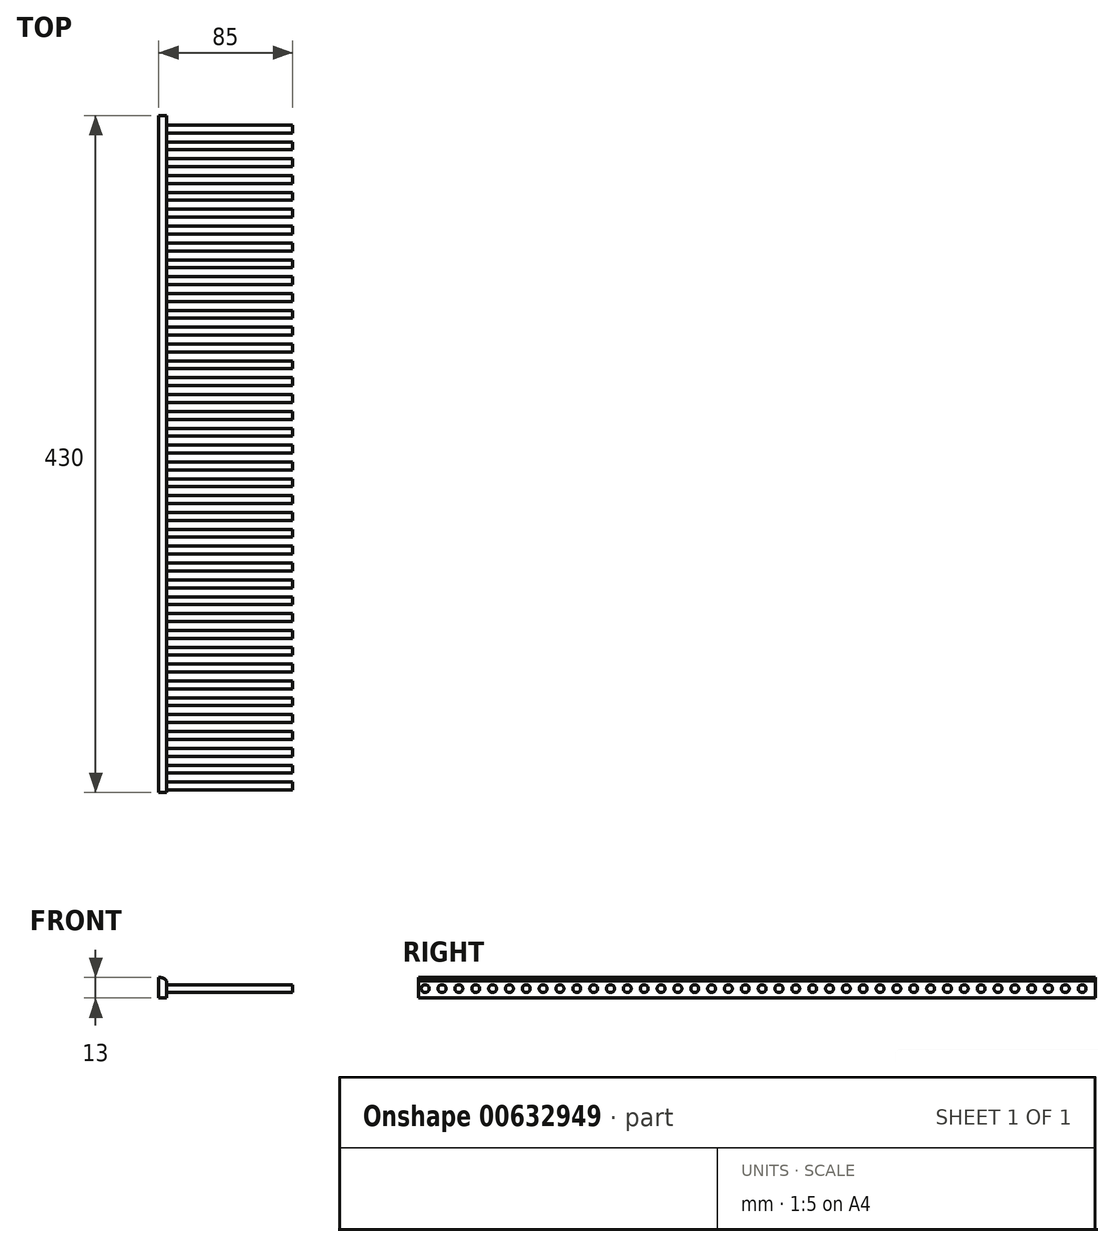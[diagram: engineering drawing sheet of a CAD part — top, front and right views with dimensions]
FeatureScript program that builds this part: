
annotation { "Feature Type Name" : "Feature", "Feature Type Description" : "" }
export const myFeature = defineFeature(function(context is Context, id is Id, definition is map)
    precondition{}
    {
        {
            var Q0;
            Q0=qCreatedBy(makeId("Right.planeOp"),FACE);
            var sketch = newSketch(context, id + "F0", { "sketchPlane" : qUnion([Q0])});
            skLineSegment(sketch, "E0.bottom", {"start": v(-215, 10.84) * mm, "end": v(215, 10.84) * mm});
            skLineSegment(sketch, "E0.top", {"start": v(-215, -2.16) * mm, "end": v(215, -2.16) * mm});
            skLineSegment(sketch, "E0.left", {"start": v(-215, 10.84) * mm, "end": v(-215, -2.16) * mm});
            skLineSegment(sketch, "E0.right", {"start": v(215, 10.84) * mm, "end": v(215, -2.16) * mm});
            skLineSegment(sketch, "E1", {"start": v(-215, 3.84) * mm, "end": v(215, 3.84) * mm, "construction": true});
            skCircle(sketch, "E2", {"center": v(206.5, 3.84) * mm, "radius": 2.5 * mm});
            skCircle(sketch, "E3", {"center": v(195.8, 3.84) * mm, "radius": 2.5 * mm});
            skCircle(sketch, "E4", {"center": v(185.1, 3.84) * mm, "radius": 2.5 * mm});
            skCircle(sketch, "E5", {"center": v(174.4, 3.84) * mm, "radius": 2.5 * mm});
            skCircle(sketch, "E6", {"center": v(163.7, 3.84) * mm, "radius": 2.5 * mm});
            skCircle(sketch, "E7", {"center": v(153, 3.84) * mm, "radius": 2.5 * mm});
            skCircle(sketch, "E8", {"center": v(142.3, 3.84) * mm, "radius": 2.5 * mm});
            skCircle(sketch, "E9", {"center": v(131.6, 3.84) * mm, "radius": 2.5 * mm});
            skCircle(sketch, "E10", {"center": v(120.9, 3.84) * mm, "radius": 2.5 * mm});
            skCircle(sketch, "E11", {"center": v(110.2, 3.84) * mm, "radius": 2.5 * mm});
            skCircle(sketch, "E12", {"center": v(99.5, 3.84) * mm, "radius": 2.5 * mm});
            skCircle(sketch, "E13", {"center": v(88.8, 3.84) * mm, "radius": 2.5 * mm});
            skCircle(sketch, "E14", {"center": v(78.1, 3.84) * mm, "radius": 2.5 * mm});
            skCircle(sketch, "E15", {"center": v(67.4, 3.84) * mm, "radius": 2.5 * mm});
            skCircle(sketch, "E16", {"center": v(56.7, 3.84) * mm, "radius": 2.5 * mm});
            skCircle(sketch, "E17", {"center": v(46, 3.84) * mm, "radius": 2.5 * mm});
            skCircle(sketch, "E18", {"center": v(35.3, 3.84) * mm, "radius": 2.5 * mm});
            skCircle(sketch, "E19", {"center": v(24.6, 3.84) * mm, "radius": 2.5 * mm});
            skCircle(sketch, "E20", {"center": v(13.9, 3.84) * mm, "radius": 2.5 * mm});
            skCircle(sketch, "E21", {"center": v(3.2, 3.84) * mm, "radius": 2.5 * mm});
            skCircle(sketch, "E22", {"center": v(-7.5, 3.84) * mm, "radius": 2.5 * mm});
            skCircle(sketch, "E23", {"center": v(-18.2, 3.84) * mm, "radius": 2.5 * mm});
            skCircle(sketch, "E24", {"center": v(-28.9, 3.84) * mm, "radius": 2.5 * mm});
            skCircle(sketch, "E25", {"center": v(-39.6, 3.84) * mm, "radius": 2.5 * mm});
            skCircle(sketch, "E26", {"center": v(-50.3, 3.84) * mm, "radius": 2.5 * mm});
            skCircle(sketch, "E27", {"center": v(-61, 3.84) * mm, "radius": 2.5 * mm});
            skCircle(sketch, "E28", {"center": v(-71.7, 3.84) * mm, "radius": 2.5 * mm});
            skCircle(sketch, "E29", {"center": v(-82.4, 3.84) * mm, "radius": 2.5 * mm});
            skCircle(sketch, "E30", {"center": v(-93.1, 3.84) * mm, "radius": 2.5 * mm});
            skCircle(sketch, "E31", {"center": v(-103.8, 3.84) * mm, "radius": 2.5 * mm});
            skCircle(sketch, "E32", {"center": v(-114.5, 3.84) * mm, "radius": 2.5 * mm});
            skCircle(sketch, "E33", {"center": v(-125.2, 3.84) * mm, "radius": 2.5 * mm});
            skCircle(sketch, "E34", {"center": v(-135.9, 3.84) * mm, "radius": 2.5 * mm});
            skCircle(sketch, "E35", {"center": v(-146.6, 3.84) * mm, "radius": 2.5 * mm});
            skCircle(sketch, "E36", {"center": v(-157.3, 3.84) * mm, "radius": 2.5 * mm});
            skCircle(sketch, "E37", {"center": v(-168, 3.84) * mm, "radius": 2.5 * mm});
            skCircle(sketch, "E38", {"center": v(-178.7, 3.84) * mm, "radius": 2.5 * mm});
            skCircle(sketch, "E39", {"center": v(-189.4, 3.84) * mm, "radius": 2.5 * mm});
            skCircle(sketch, "E40", {"center": v(-200.1, 3.84) * mm, "radius": 2.5 * mm});
            skCircle(sketch, "E41", {"center": v(-210.8, 3.84) * mm, "radius": 2.5 * mm});
            skSolve(sketch);
        }
        {
            var Q0;
            Q0=makeQuery(id+"F0.imprint","IMPRINT",FACE,{"disambiguationData":[TD([[makeQuery(id+"F0.imprint","IMPRINT",EDGE,{"derivedFrom":sQuery(id+"F0.wireOp",EDGE,"E40")}),1.0]])]});
            var Q1;
            Q1=makeQuery(id+"F0.imprint","IMPRINT",FACE,{"disambiguationData":[TD([[makeQuery(id+"F0.imprint","IMPRINT",EDGE,{"derivedFrom":sQuery(id+"F0.wireOp",EDGE,"E41")}),1.0]])]});
            var Q2;
            Q2=makeQuery(id+"F0.imprint","IMPRINT",FACE,{"disambiguationData":[TD([[makeQuery(id+"F0.imprint","IMPRINT",EDGE,{"derivedFrom":sQuery(id+"F0.wireOp",EDGE,"E39")}),1.0]])]});
            var Q3;
            Q3=makeQuery(id+"F0.imprint","IMPRINT",FACE,{"disambiguationData":[TD([[makeQuery(id+"F0.imprint","IMPRINT",EDGE,{"derivedFrom":sQuery(id+"F0.wireOp",EDGE,"E38")}),1.0]])]});
            var Q4;
            Q4=makeQuery(id+"F0.imprint","IMPRINT",FACE,{"disambiguationData":[TD([[makeQuery(id+"F0.imprint","IMPRINT",EDGE,{"derivedFrom":sQuery(id+"F0.wireOp",EDGE,"E37")}),1.0]])]});
            var Q5;
            Q5=makeQuery(id+"F0.imprint","IMPRINT",FACE,{"disambiguationData":[TD([[makeQuery(id+"F0.imprint","IMPRINT",EDGE,{"derivedFrom":sQuery(id+"F0.wireOp",EDGE,"E36")}),1.0]])]});
            var Q6;
            Q6=makeQuery(id+"F0.imprint","IMPRINT",FACE,{"disambiguationData":[TD([[makeQuery(id+"F0.imprint","IMPRINT",EDGE,{"derivedFrom":sQuery(id+"F0.wireOp",EDGE,"E35")}),1.0]])]});
            var Q7;
            Q7=makeQuery(id+"F0.imprint","IMPRINT",FACE,{"disambiguationData":[TD([[makeQuery(id+"F0.imprint","IMPRINT",EDGE,{"derivedFrom":sQuery(id+"F0.wireOp",EDGE,"E34")}),1.0]])]});
            var Q8;
            Q8=makeQuery(id+"F0.imprint","IMPRINT",FACE,{"disambiguationData":[TD([[makeQuery(id+"F0.imprint","IMPRINT",EDGE,{"derivedFrom":sQuery(id+"F0.wireOp",EDGE,"E33")}),1.0]])]});
            var Q9;
            Q9=makeQuery(id+"F0.imprint","IMPRINT",FACE,{"disambiguationData":[TD([[makeQuery(id+"F0.imprint","IMPRINT",EDGE,{"derivedFrom":sQuery(id+"F0.wireOp",EDGE,"E32")}),1.0]])]});
            var Q10;
            Q10=makeQuery(id+"F0.imprint","IMPRINT",FACE,{"disambiguationData":[TD([[makeQuery(id+"F0.imprint","IMPRINT",EDGE,{"derivedFrom":sQuery(id+"F0.wireOp",EDGE,"E31")}),1.0]])]});
            var Q11;
            Q11=makeQuery(id+"F0.imprint","IMPRINT",FACE,{"disambiguationData":[TD([[makeQuery(id+"F0.imprint","IMPRINT",EDGE,{"derivedFrom":sQuery(id+"F0.wireOp",EDGE,"E30")}),1.0]])]});
            var Q12;
            Q12=makeQuery(id+"F0.imprint","IMPRINT",FACE,{"disambiguationData":[TD([[makeQuery(id+"F0.imprint","IMPRINT",EDGE,{"derivedFrom":sQuery(id+"F0.wireOp",EDGE,"E29")}),1.0]])]});
            var Q13;
            Q13=makeQuery(id+"F0.imprint","IMPRINT",FACE,{"disambiguationData":[TD([[makeQuery(id+"F0.imprint","IMPRINT",EDGE,{"derivedFrom":sQuery(id+"F0.wireOp",EDGE,"E28")}),1.0]])]});
            var Q14;
            Q14=makeQuery(id+"F0.imprint","IMPRINT",FACE,{"disambiguationData":[TD([[makeQuery(id+"F0.imprint","IMPRINT",EDGE,{"derivedFrom":sQuery(id+"F0.wireOp",EDGE,"E27")}),1.0]])]});
            var Q15;
            Q15=makeQuery(id+"F0.imprint","IMPRINT",FACE,{"disambiguationData":[TD([[makeQuery(id+"F0.imprint","IMPRINT",EDGE,{"derivedFrom":sQuery(id+"F0.wireOp",EDGE,"E26")}),1.0]])]});
            var Q16;
            Q16=makeQuery(id+"F0.imprint","IMPRINT",FACE,{"disambiguationData":[TD([[makeQuery(id+"F0.imprint","IMPRINT",EDGE,{"derivedFrom":sQuery(id+"F0.wireOp",EDGE,"E25")}),1.0]])]});
            var Q17;
            Q17=makeQuery(id+"F0.imprint","IMPRINT",FACE,{"disambiguationData":[TD([[makeQuery(id+"F0.imprint","IMPRINT",EDGE,{"derivedFrom":sQuery(id+"F0.wireOp",EDGE,"E24")}),1.0]])]});
            var Q18;
            Q18=makeQuery(id+"F0.imprint","IMPRINT",FACE,{"disambiguationData":[TD([[makeQuery(id+"F0.imprint","IMPRINT",EDGE,{"derivedFrom":sQuery(id+"F0.wireOp",EDGE,"E23")}),1.0]])]});
            var Q19;
            Q19=makeQuery(id+"F0.imprint","IMPRINT",FACE,{"disambiguationData":[TD([[makeQuery(id+"F0.imprint","IMPRINT",EDGE,{"derivedFrom":sQuery(id+"F0.wireOp",EDGE,"E22")}),1.0]])]});
            var Q20;
            Q20=makeQuery(id+"F0.imprint","IMPRINT",FACE,{"disambiguationData":[TD([[makeQuery(id+"F0.imprint","IMPRINT",EDGE,{"derivedFrom":sQuery(id+"F0.wireOp",EDGE,"E21")}),1.0]])]});
            var Q21;
            Q21=makeQuery(id+"F0.imprint","IMPRINT",FACE,{"disambiguationData":[TD([[makeQuery(id+"F0.imprint","IMPRINT",EDGE,{"derivedFrom":sQuery(id+"F0.wireOp",EDGE,"E20")}),1.0]])]});
            var Q22;
            Q22=makeQuery(id+"F0.imprint","IMPRINT",FACE,{"disambiguationData":[TD([[makeQuery(id+"F0.imprint","IMPRINT",EDGE,{"derivedFrom":sQuery(id+"F0.wireOp",EDGE,"E19")}),1.0]])]});
            var Q23;
            Q23=makeQuery(id+"F0.imprint","IMPRINT",FACE,{"disambiguationData":[TD([[makeQuery(id+"F0.imprint","IMPRINT",EDGE,{"derivedFrom":sQuery(id+"F0.wireOp",EDGE,"E18")}),1.0]])]});
            var Q24;
            Q24=makeQuery(id+"F0.imprint","IMPRINT",FACE,{"disambiguationData":[TD([[makeQuery(id+"F0.imprint","IMPRINT",EDGE,{"derivedFrom":sQuery(id+"F0.wireOp",EDGE,"E17")}),1.0]])]});
            var Q25;
            Q25=makeQuery(id+"F0.imprint","IMPRINT",FACE,{"disambiguationData":[TD([[makeQuery(id+"F0.imprint","IMPRINT",EDGE,{"derivedFrom":sQuery(id+"F0.wireOp",EDGE,"E16")}),1.0]])]});
            var Q26;
            Q26=makeQuery(id+"F0.imprint","IMPRINT",FACE,{"disambiguationData":[TD([[makeQuery(id+"F0.imprint","IMPRINT",EDGE,{"derivedFrom":sQuery(id+"F0.wireOp",EDGE,"E15")}),1.0]])]});
            var Q27;
            Q27=makeQuery(id+"F0.imprint","IMPRINT",FACE,{"disambiguationData":[TD([[makeQuery(id+"F0.imprint","IMPRINT",EDGE,{"derivedFrom":sQuery(id+"F0.wireOp",EDGE,"E14")}),1.0]])]});
            var Q28;
            Q28=makeQuery(id+"F0.imprint","IMPRINT",FACE,{"disambiguationData":[TD([[makeQuery(id+"F0.imprint","IMPRINT",EDGE,{"derivedFrom":sQuery(id+"F0.wireOp",EDGE,"E13")}),1.0]])]});
            var Q29;
            Q29=makeQuery(id+"F0.imprint","IMPRINT",FACE,{"disambiguationData":[TD([[makeQuery(id+"F0.imprint","IMPRINT",EDGE,{"derivedFrom":sQuery(id+"F0.wireOp",EDGE,"E12")}),1.0]])]});
            var Q30;
            Q30=makeQuery(id+"F0.imprint","IMPRINT",FACE,{"disambiguationData":[TD([[makeQuery(id+"F0.imprint","IMPRINT",EDGE,{"derivedFrom":sQuery(id+"F0.wireOp",EDGE,"E11")}),1.0]])]});
            var Q31;
            Q31=makeQuery(id+"F0.imprint","IMPRINT",FACE,{"disambiguationData":[TD([[makeQuery(id+"F0.imprint","IMPRINT",EDGE,{"derivedFrom":sQuery(id+"F0.wireOp",EDGE,"E10")}),1.0]])]});
            var Q32;
            Q32=makeQuery(id+"F0.imprint","IMPRINT",FACE,{"disambiguationData":[TD([[makeQuery(id+"F0.imprint","IMPRINT",EDGE,{"derivedFrom":sQuery(id+"F0.wireOp",EDGE,"E9")}),1.0]])]});
            var Q33;
            Q33=makeQuery(id+"F0.imprint","IMPRINT",FACE,{"disambiguationData":[TD([[makeQuery(id+"F0.imprint","IMPRINT",EDGE,{"derivedFrom":sQuery(id+"F0.wireOp",EDGE,"E8")}),1.0]])]});
            var Q34;
            Q34=makeQuery(id+"F0.imprint","IMPRINT",FACE,{"disambiguationData":[TD([[makeQuery(id+"F0.imprint","IMPRINT",EDGE,{"derivedFrom":sQuery(id+"F0.wireOp",EDGE,"E7")}),1.0]])]});
            var Q35;
            Q35=makeQuery(id+"F0.imprint","IMPRINT",FACE,{"disambiguationData":[TD([[makeQuery(id+"F0.imprint","IMPRINT",EDGE,{"derivedFrom":sQuery(id+"F0.wireOp",EDGE,"E6")}),1.0]])]});
            var Q36;
            Q36=makeQuery(id+"F0.imprint","IMPRINT",FACE,{"disambiguationData":[TD([[makeQuery(id+"F0.imprint","IMPRINT",EDGE,{"derivedFrom":sQuery(id+"F0.wireOp",EDGE,"E5")}),1.0]])]});
            var Q37;
            Q37=makeQuery(id+"F0.imprint","IMPRINT",FACE,{"disambiguationData":[TD([[makeQuery(id+"F0.imprint","IMPRINT",EDGE,{"derivedFrom":sQuery(id+"F0.wireOp",EDGE,"E4")}),1.0]])]});
            var Q38;
            Q38=makeQuery(id+"F0.imprint","IMPRINT",FACE,{"disambiguationData":[TD([[makeQuery(id+"F0.imprint","IMPRINT",EDGE,{"derivedFrom":sQuery(id+"F0.wireOp",EDGE,"E3")}),1.0]])]});
            var Q39;
            Q39=makeQuery(id+"F0.imprint","IMPRINT",FACE,{"disambiguationData":[TD([[makeQuery(id+"F0.imprint","IMPRINT",EDGE,{"derivedFrom":sQuery(id+"F0.wireOp",EDGE,"E2")}),1.0]])]});
            extrude(context, id + "F1", {"entities" : qUnion([Q0, Q1, Q2, Q3, Q4, Q5, Q6, Q7, Q8, Q9, Q10, Q11, Q12, Q13, Q14, Q15, Q16, Q17, Q18, Q19, Q20, Q21, Q22, Q23, Q24, Q25, Q26, Q27, Q28, Q29, Q30, Q31, Q32, Q33, Q34, Q35, Q36, Q37, Q38, Q39]), "depth" : 80 * mm, "offsetDistance" : 25 * mm});
        }
        {
            var Q0;
            Q0=makeQuery(id+"F0.imprint","IMPRINT",FACE,{"disambiguationData":[TD([[makeQuery(id+"F0.imprint","IMPRINT",EDGE,{"derivedFrom":sQuery(id+"F0.wireOp",EDGE,"E0.bottom")}),-1.0]])]});
            var Q1;
            Q1=makeQuery(id+"F0.imprint","IMPRINT",FACE,{"disambiguationData":[TD([[makeQuery(id+"F0.imprint","IMPRINT",EDGE,{"derivedFrom":sQuery(id+"F0.wireOp",EDGE,"E2")}),1.0]])]});
            var Q2;
            Q2=makeQuery(id+"F0.imprint","IMPRINT",FACE,{"disambiguationData":[TD([[makeQuery(id+"F0.imprint","IMPRINT",EDGE,{"derivedFrom":sQuery(id+"F0.wireOp",EDGE,"E3")}),1.0]])]});
            var Q3;
            Q3=makeQuery(id+"F0.imprint","IMPRINT",FACE,{"disambiguationData":[TD([[makeQuery(id+"F0.imprint","IMPRINT",EDGE,{"derivedFrom":sQuery(id+"F0.wireOp",EDGE,"E4")}),1.0]])]});
            var Q4;
            Q4=makeQuery(id+"F0.imprint","IMPRINT",FACE,{"disambiguationData":[TD([[makeQuery(id+"F0.imprint","IMPRINT",EDGE,{"derivedFrom":sQuery(id+"F0.wireOp",EDGE,"E5")}),1.0]])]});
            var Q5;
            Q5=makeQuery(id+"F0.imprint","IMPRINT",FACE,{"disambiguationData":[TD([[makeQuery(id+"F0.imprint","IMPRINT",EDGE,{"derivedFrom":sQuery(id+"F0.wireOp",EDGE,"E6")}),1.0]])]});
            var Q6;
            Q6=makeQuery(id+"F0.imprint","IMPRINT",FACE,{"disambiguationData":[TD([[makeQuery(id+"F0.imprint","IMPRINT",EDGE,{"derivedFrom":sQuery(id+"F0.wireOp",EDGE,"E7")}),1.0]])]});
            var Q7;
            Q7=makeQuery(id+"F0.imprint","IMPRINT",FACE,{"disambiguationData":[TD([[makeQuery(id+"F0.imprint","IMPRINT",EDGE,{"derivedFrom":sQuery(id+"F0.wireOp",EDGE,"E8")}),1.0]])]});
            var Q8;
            Q8=makeQuery(id+"F0.imprint","IMPRINT",FACE,{"disambiguationData":[TD([[makeQuery(id+"F0.imprint","IMPRINT",EDGE,{"derivedFrom":sQuery(id+"F0.wireOp",EDGE,"E9")}),1.0]])]});
            var Q9;
            Q9=makeQuery(id+"F0.imprint","IMPRINT",FACE,{"disambiguationData":[TD([[makeQuery(id+"F0.imprint","IMPRINT",EDGE,{"derivedFrom":sQuery(id+"F0.wireOp",EDGE,"E10")}),1.0]])]});
            var Q10;
            Q10=makeQuery(id+"F0.imprint","IMPRINT",FACE,{"disambiguationData":[TD([[makeQuery(id+"F0.imprint","IMPRINT",EDGE,{"derivedFrom":sQuery(id+"F0.wireOp",EDGE,"E11")}),1.0]])]});
            var Q11;
            Q11=makeQuery(id+"F0.imprint","IMPRINT",FACE,{"disambiguationData":[TD([[makeQuery(id+"F0.imprint","IMPRINT",EDGE,{"derivedFrom":sQuery(id+"F0.wireOp",EDGE,"E12")}),1.0]])]});
            var Q12;
            Q12=makeQuery(id+"F0.imprint","IMPRINT",FACE,{"disambiguationData":[TD([[makeQuery(id+"F0.imprint","IMPRINT",EDGE,{"derivedFrom":sQuery(id+"F0.wireOp",EDGE,"E13")}),1.0]])]});
            var Q13;
            Q13=makeQuery(id+"F0.imprint","IMPRINT",FACE,{"disambiguationData":[TD([[makeQuery(id+"F0.imprint","IMPRINT",EDGE,{"derivedFrom":sQuery(id+"F0.wireOp",EDGE,"E14")}),1.0]])]});
            var Q14;
            Q14=makeQuery(id+"F0.imprint","IMPRINT",FACE,{"disambiguationData":[TD([[makeQuery(id+"F0.imprint","IMPRINT",EDGE,{"derivedFrom":sQuery(id+"F0.wireOp",EDGE,"E15")}),1.0]])]});
            var Q15;
            Q15=makeQuery(id+"F0.imprint","IMPRINT",FACE,{"disambiguationData":[TD([[makeQuery(id+"F0.imprint","IMPRINT",EDGE,{"derivedFrom":sQuery(id+"F0.wireOp",EDGE,"E16")}),1.0]])]});
            var Q16;
            Q16=makeQuery(id+"F0.imprint","IMPRINT",FACE,{"disambiguationData":[TD([[makeQuery(id+"F0.imprint","IMPRINT",EDGE,{"derivedFrom":sQuery(id+"F0.wireOp",EDGE,"E17")}),1.0]])]});
            var Q17;
            Q17=makeQuery(id+"F0.imprint","IMPRINT",FACE,{"disambiguationData":[TD([[makeQuery(id+"F0.imprint","IMPRINT",EDGE,{"derivedFrom":sQuery(id+"F0.wireOp",EDGE,"E18")}),1.0]])]});
            var Q18;
            Q18=makeQuery(id+"F0.imprint","IMPRINT",FACE,{"disambiguationData":[TD([[makeQuery(id+"F0.imprint","IMPRINT",EDGE,{"derivedFrom":sQuery(id+"F0.wireOp",EDGE,"E19")}),1.0]])]});
            var Q19;
            Q19=makeQuery(id+"F0.imprint","IMPRINT",FACE,{"disambiguationData":[TD([[makeQuery(id+"F0.imprint","IMPRINT",EDGE,{"derivedFrom":sQuery(id+"F0.wireOp",EDGE,"E20")}),1.0]])]});
            var Q20;
            Q20=makeQuery(id+"F0.imprint","IMPRINT",FACE,{"disambiguationData":[TD([[makeQuery(id+"F0.imprint","IMPRINT",EDGE,{"derivedFrom":sQuery(id+"F0.wireOp",EDGE,"E21")}),1.0]])]});
            var Q21;
            Q21=makeQuery(id+"F0.imprint","IMPRINT",FACE,{"disambiguationData":[TD([[makeQuery(id+"F0.imprint","IMPRINT",EDGE,{"derivedFrom":sQuery(id+"F0.wireOp",EDGE,"E22")}),1.0]])]});
            var Q22;
            Q22=makeQuery(id+"F0.imprint","IMPRINT",FACE,{"disambiguationData":[TD([[makeQuery(id+"F0.imprint","IMPRINT",EDGE,{"derivedFrom":sQuery(id+"F0.wireOp",EDGE,"E23")}),1.0]])]});
            var Q23;
            Q23=makeQuery(id+"F0.imprint","IMPRINT",FACE,{"disambiguationData":[TD([[makeQuery(id+"F0.imprint","IMPRINT",EDGE,{"derivedFrom":sQuery(id+"F0.wireOp",EDGE,"E24")}),1.0]])]});
            var Q24;
            Q24=makeQuery(id+"F0.imprint","IMPRINT",FACE,{"disambiguationData":[TD([[makeQuery(id+"F0.imprint","IMPRINT",EDGE,{"derivedFrom":sQuery(id+"F0.wireOp",EDGE,"E25")}),1.0]])]});
            var Q25;
            Q25=makeQuery(id+"F0.imprint","IMPRINT",FACE,{"disambiguationData":[TD([[makeQuery(id+"F0.imprint","IMPRINT",EDGE,{"derivedFrom":sQuery(id+"F0.wireOp",EDGE,"E26")}),1.0]])]});
            var Q26;
            Q26=makeQuery(id+"F0.imprint","IMPRINT",FACE,{"disambiguationData":[TD([[makeQuery(id+"F0.imprint","IMPRINT",EDGE,{"derivedFrom":sQuery(id+"F0.wireOp",EDGE,"E27")}),1.0]])]});
            var Q27;
            Q27=makeQuery(id+"F0.imprint","IMPRINT",FACE,{"disambiguationData":[TD([[makeQuery(id+"F0.imprint","IMPRINT",EDGE,{"derivedFrom":sQuery(id+"F0.wireOp",EDGE,"E28")}),1.0]])]});
            var Q28;
            Q28=makeQuery(id+"F0.imprint","IMPRINT",FACE,{"disambiguationData":[TD([[makeQuery(id+"F0.imprint","IMPRINT",EDGE,{"derivedFrom":sQuery(id+"F0.wireOp",EDGE,"E29")}),1.0]])]});
            var Q29;
            Q29=makeQuery(id+"F0.imprint","IMPRINT",FACE,{"disambiguationData":[TD([[makeQuery(id+"F0.imprint","IMPRINT",EDGE,{"derivedFrom":sQuery(id+"F0.wireOp",EDGE,"E30")}),1.0]])]});
            var Q30;
            Q30=makeQuery(id+"F0.imprint","IMPRINT",FACE,{"disambiguationData":[TD([[makeQuery(id+"F0.imprint","IMPRINT",EDGE,{"derivedFrom":sQuery(id+"F0.wireOp",EDGE,"E31")}),1.0]])]});
            var Q31;
            Q31=makeQuery(id+"F0.imprint","IMPRINT",FACE,{"disambiguationData":[TD([[makeQuery(id+"F0.imprint","IMPRINT",EDGE,{"derivedFrom":sQuery(id+"F0.wireOp",EDGE,"E32")}),1.0]])]});
            var Q32;
            Q32=makeQuery(id+"F0.imprint","IMPRINT",FACE,{"disambiguationData":[TD([[makeQuery(id+"F0.imprint","IMPRINT",EDGE,{"derivedFrom":sQuery(id+"F0.wireOp",EDGE,"E33")}),1.0]])]});
            var Q33;
            Q33=makeQuery(id+"F0.imprint","IMPRINT",FACE,{"disambiguationData":[TD([[makeQuery(id+"F0.imprint","IMPRINT",EDGE,{"derivedFrom":sQuery(id+"F0.wireOp",EDGE,"E34")}),1.0]])]});
            var Q34;
            Q34=makeQuery(id+"F0.imprint","IMPRINT",FACE,{"disambiguationData":[TD([[makeQuery(id+"F0.imprint","IMPRINT",EDGE,{"derivedFrom":sQuery(id+"F0.wireOp",EDGE,"E35")}),1.0]])]});
            var Q35;
            Q35=makeQuery(id+"F0.imprint","IMPRINT",FACE,{"disambiguationData":[TD([[makeQuery(id+"F0.imprint","IMPRINT",EDGE,{"derivedFrom":sQuery(id+"F0.wireOp",EDGE,"E36")}),1.0]])]});
            var Q36;
            Q36=makeQuery(id+"F0.imprint","IMPRINT",FACE,{"disambiguationData":[TD([[makeQuery(id+"F0.imprint","IMPRINT",EDGE,{"derivedFrom":sQuery(id+"F0.wireOp",EDGE,"E37")}),1.0]])]});
            var Q37;
            Q37=makeQuery(id+"F0.imprint","IMPRINT",FACE,{"disambiguationData":[TD([[makeQuery(id+"F0.imprint","IMPRINT",EDGE,{"derivedFrom":sQuery(id+"F0.wireOp",EDGE,"E38")}),1.0]])]});
            var Q38;
            Q38=makeQuery(id+"F0.imprint","IMPRINT",FACE,{"disambiguationData":[TD([[makeQuery(id+"F0.imprint","IMPRINT",EDGE,{"derivedFrom":sQuery(id+"F0.wireOp",EDGE,"E39")}),1.0]])]});
            var Q39;
            Q39=makeQuery(id+"F0.imprint","IMPRINT",FACE,{"disambiguationData":[TD([[makeQuery(id+"F0.imprint","IMPRINT",EDGE,{"derivedFrom":sQuery(id+"F0.wireOp",EDGE,"E40")}),1.0]])]});
            var Q40;
            Q40=makeQuery(id+"F0.imprint","IMPRINT",FACE,{"disambiguationData":[TD([[makeQuery(id+"F0.imprint","IMPRINT",EDGE,{"derivedFrom":sQuery(id+"F0.wireOp",EDGE,"E41")}),1.0]])]});
            extrude(context, id + "F2", {"entities" : qUnion([Q0, Q1, Q2, Q3, Q4, Q5, Q6, Q7, Q8, Q9, Q10, Q11, Q12, Q13, Q14, Q15, Q16, Q17, Q18, Q19, Q20, Q21, Q22, Q23, Q24, Q25, Q26, Q27, Q28, Q29, Q30, Q31, Q32, Q33, Q34, Q35, Q36, Q37, Q38, Q39, Q40]), "oppositeDirection" : true, "depth" : 5 * mm, "offsetDistance" : 25 * mm});
        }
        {
            var Q0;
            Q0=makeQuery(id+"F2.opExtrude","CAP_EDGE",EDGE,{"disambiguationData":[OSD([sQuery(id+"F0.wireOp",EDGE,"E0.bottom")])],"isStart":true});
            chamfer(context, id + "F3", {"entities" : qUnion([Q0]), "width" : 2 * mm, "tangentPropagation" : true});
        }
        {
            var Q0;
            {var subQ0=sQuery(id+"F0.wireOp",EDGE,"E0.bottom");Q0=makeQuery(id+"F3.opChamfer","BLEND_EDGE",EDGE,{"blendedFrom":[makeQuery(id+"F2.opExtrude","CAP_EDGE",EDGE,{"disambiguationData":[OSD([subQ0])],"isStart":true}),makeQuery(id+"F2.opExtrude","SWEPT_FACE",FACE,{"disambiguationData":[OSD([subQ0])]})],"blendedInto":[makeQuery(id+"F2.opExtrude","SWEPT_FACE",FACE,{"disambiguationData":[OSD([subQ0])]})]});}
            fillet(context, id + "F4", {"entities" : qUnion([Q0]), "radius" : 5 * mm, "tangentPropagation" : true, "allowEdgeOverflow" : false});
        }
    });
